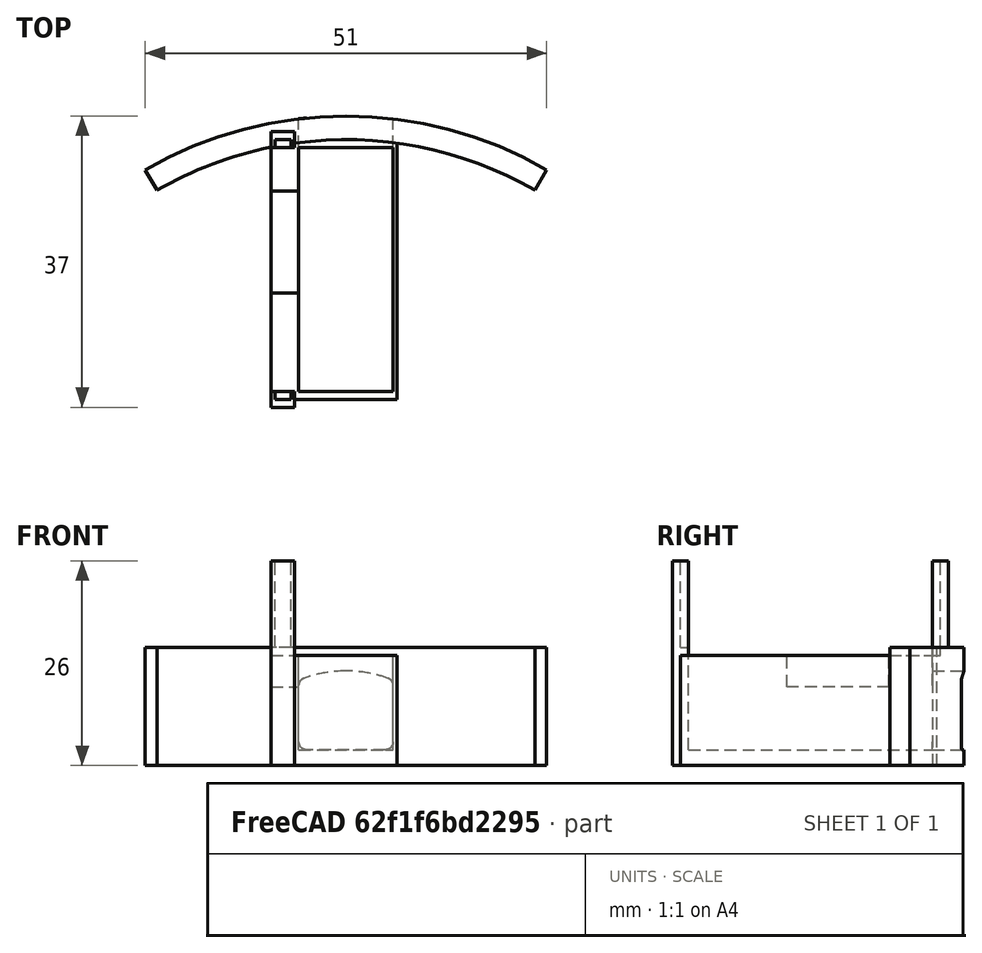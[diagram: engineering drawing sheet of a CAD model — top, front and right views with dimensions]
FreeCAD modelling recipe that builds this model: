
FCSTD DOCUMENT  (FreeCAD 0.16R4924 (Git))
Label: interior_servo_bay_v4
License: All rights reserved
LicenseURL: http://en.wikipedia.org/wiki/All_rights_reserved
objects: Part::Cut×6, Part::Box×6, Part::MultiFuse×3, Part::Cylinder×2, Part::Feature×2, Part::Extrusion×2, App::MeasureDistance×2, Part::Thickness×1
note: 22 computed .brp shape members not serialized (recipe doc carries the construction recipe); baked Part::Feature solids carry a one-line shape summary decoded from their .brp

FEATURE [Part::Cylinder] Cylinder  label="bottle_wall"
  Angle = 60
  Height = 15
  Placement = pos=(8.5,-7,0) rot=(0,0,1;1.0472rad)
  Radius = 51
FEATURE [Part::Cylinder] Cylinder001  label="bottle_wall001"
  Angle = 60
  Height = 15
  Placement = pos=(8.5,-7,0) rot=(0,0,1;1.0472rad)
  Radius = 48
FEATURE [Part::Cut] Cut  label="bottle_wall_composite"
  Base = -> Cylinder
  Placement = pos=(0,-2,0) rot=(0,0,1;0rad)
  Tool = -> Cylinder001
FEATURE [Part::Feature] Common_cs  label="pin_cs"
  Placement = pos=(3.5,35,2) rot=(0,0,1;0rad)
  shape: bbox 10 x 2e-07 x 8 mm, 0 faces, 0 solids (baked)
FEATURE [Part::Extrusion] Extrude
  Base = -> Common_cs
  Dir = (0,5,0)
  Solid = true
FEATURE [Part::Thickness] Thickness
  Faces = -> Extrude [Face7]
  Intersection = false
  Join = 0
  Mode = 0
  SelfIntersection = false
  Value = 1
FEATURE [Part::Feature] Common_cs001  label="pin_cs001"
  Placement = pos=(3.5,35,2) rot=(0,0,1;0rad)
  shape: bbox 10 x 2e-07 x 8 mm, 0 faces, 0 solids (baked)
FEATURE [Part::Extrusion] Extrude001
  Base = -> Common_cs001
  Dir = (0,5,0)
  Solid = true
FEATURE [Part::MultiFuse] Fusion  label="bolt_bottle_side_opening"
  Placement = pos=(0,-7,1) rot=(0,0,1;0rad)
  Shapes = -> [Thickness,Extrude,Extrude001]
FEATURE [Part::Box] Box  label="pullBay"
  Height = 15
  Length = 12
  Placement = pos=(2.5,7,2) rot=(0,0,1;0rad)
  Width = 31
FEATURE [Part::Box] Box001  label="Case"
  Height = 14
  Length = 13
  Placement = pos=(2,6,0) rot=(0,0,1;0rad)
  Width = 34
FEATURE [Part::Cut] Cut001  label="cut bay from case"
  Base = -> Box001
  Tool = -> Box
FEATURE [Part::MultiFuse] Fusion001  label="wall plus case"
  Shapes = -> [Cut,Cut001]
FEATURE [Part::Cut] Cut002  label="hole cut out of case"
  Base = -> Fusion001
  Tool = -> Fusion
FEATURE [Part::Box] Box002  label="slot wall"
  Height = 26
  Length = 3
  Placement = pos=(-1,5,0) rot=(0,0,1;0rad)
  Width = 35
FEATURE [Part::Box] Box003  label="slot wall cutout1"
  Height = 11.2
  Length = 2
  Placement = pos=(-0.5,6,15) rot=(0,0,1;0rad)
  Width = 33
FEATURE [Part::Cut] Cut003
  Base = -> Box002
  Tool = -> Box003
FEATURE [Part::Box] Box004  label="slot wall cutout2"
  Height = 14
  Length = 3
  Placement = pos=(-1,7,14) rot=(0,0,1;0rad)
  Width = 31
FEATURE [Part::Cut] Cut004  label="wall slot finished"
  Base = -> Cut003
  Tool = -> Box004
FEATURE [Part::MultiFuse] Fusion002
  Shapes = -> [Cut002,Cut004]
FEATURE [App::MeasureDistance] Distance  label="Distance: 33.123"
  Distance = 33.1232
  P1 = (1.15787,39.1229,26)
  P2 = (1.00961,6,26)
FEATURE [App::MeasureDistance] Distance001  label="Distance: 12.028"
  Distance = 12.0279
  P1 = (0,7,26)
  P2 = (0,7.81869,14)
FEATURE [Part::Box] Box005  label="servo wall cutaway"
  Height = 4
  Length = 5
  Placement = pos=(-2,19.5,10) rot=(0,0,1;0rad)
  Width = 13
FEATURE [Part::Cut] Cut005
  Base = -> Fusion002
  Tool = -> Box005
